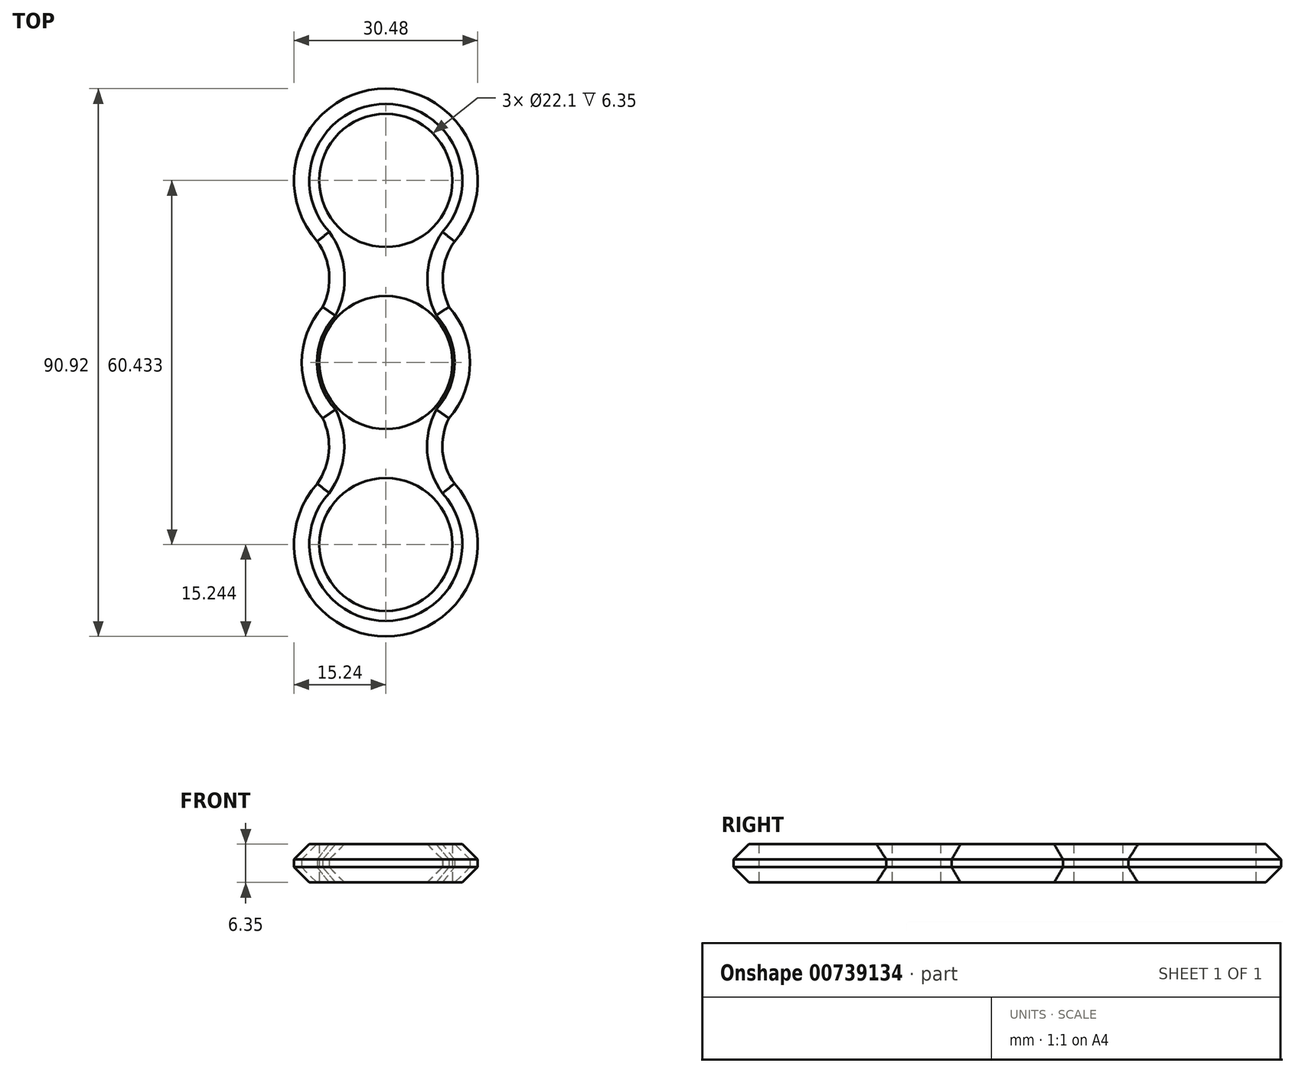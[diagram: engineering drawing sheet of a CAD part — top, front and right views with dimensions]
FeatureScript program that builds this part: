
annotation { "Feature Type Name" : "Feature", "Feature Type Description" : "" }
export const myFeature = defineFeature(function(context is Context, id is Id, definition is map)
    precondition{}
    {
        {
            var Q0;
            Q0=qCreatedBy(makeId("Top.planeOp"),FACE);
            var sketch = newSketch(context, id + "F0", { "sketchPlane" : qUnion([Q0])});
            skCircle(sketch, "E0", {"center": v(0, 0) * mm, "radius": 11.05 * mm});
            skCircle(sketch, "E1", {"center": v(0, 0) * mm, "radius": 13.97 * mm});
            skCircle(sketch, "E2", {"center": v(0, 30.22) * mm, "radius": 11.05 * mm});
            skCircle(sketch, "E3", {"center": v(0, 30.22) * mm, "radius": 15.24 * mm});
            skCircle(sketch, "E4.1.0", {"center": v(0, -30.22) * mm, "radius": 11.05 * mm});
            skCircle(sketch, "E4.1.1", {"center": v(0, -30.22) * mm, "radius": 15.24 * mm});
            skArc(sketch, "E5", {"start": v(11.4, 20.1) * mm, "mid": v(9.47, 14.79) * mm, "end": v(10.48, 9.24) * mm});
            skArc(sketch, "E6", {"start": v(-10.48, 9.24) * mm, "mid": v(-9.42, 14.8) * mm, "end": v(-11.4, 20.1) * mm});
            skArc(sketch, "E7.1.0", {"start": v(-11.4, -20.1) * mm, "mid": v(-9.47, -14.79) * mm, "end": v(-10.48, -9.24) * mm});
            skArc(sketch, "E7.1.1", {"start": v(10.48, -9.24) * mm, "mid": v(9.42, -14.8) * mm, "end": v(11.4, -20.1) * mm});
            skSolve(sketch);
        }
        {
            var Q0;
            Q0 = qSketchRegion(id + "F0", true);
            extrude(context, id + "F1", {"entities" : qUnion([Q0]), "depth" : 6.35 * mm, "offsetDistance" : 25.4 * mm});
        }
        {
            var Q0;
            Q0=makeQuery(id+"F1.opExtrude","CAP_EDGE",EDGE,{"disambiguationData":[OSD([sQuery(id+"F0.wireOp",EDGE,"E4.1.1")])],"isStart":true});
            var Q1;
            Q1=makeQuery(id+"F1.opExtrude","CAP_EDGE",EDGE,{"disambiguationData":[OSD([sQuery(id+"F0.wireOp",EDGE,"E7.1.0")])],"isStart":true});
            var Q2;
            {var subQ0=sQuery(id+"F0.wireOp",EDGE,"E1");Q2=makeQuery(id+"F1.opExtrude","CAP_EDGE",EDGE,{"disambiguationData":[OSD([subQ0]),TDD([makeQuery(id+"F0.imprint","IMPRINT",EDGE,{"disambiguationData":[TD([[makeQuery(id+"F0.imprint","INTERSECT",VERTEX,{"derivedFrom":[subQ0,sQuery(id+"F0.wireOp",EDGE,"E6")]}),-1.0]])],"derivedFrom":subQ0})])],"isStart":true});}
            var Q3;
            Q3=makeQuery(id+"F1.opExtrude","CAP_EDGE",EDGE,{"disambiguationData":[OSD([sQuery(id+"F0.wireOp",EDGE,"E6")])],"isStart":true});
            var Q4;
            Q4=makeQuery(id+"F1.opExtrude","CAP_EDGE",EDGE,{"disambiguationData":[OSD([sQuery(id+"F0.wireOp",EDGE,"E3")])],"isStart":true});
            var Q5;
            Q5=makeQuery(id+"F1.opExtrude","CAP_EDGE",EDGE,{"disambiguationData":[OSD([sQuery(id+"F0.wireOp",EDGE,"E5")])],"isStart":true});
            var Q6;
            {var subQ0=sQuery(id+"F0.wireOp",EDGE,"E1");Q6=makeQuery(id+"F1.opExtrude","CAP_EDGE",EDGE,{"disambiguationData":[OSD([subQ0]),TDD([makeQuery(id+"F0.imprint","IMPRINT",EDGE,{"disambiguationData":[TD([[makeQuery(id+"F0.imprint","INTERSECT",VERTEX,{"derivedFrom":[subQ0,sQuery(id+"F0.wireOp",EDGE,"E5")]}),1.0]])],"derivedFrom":subQ0})])],"isStart":true});}
            var Q7;
            Q7=makeQuery(id+"F1.opExtrude","CAP_EDGE",EDGE,{"disambiguationData":[OSD([sQuery(id+"F0.wireOp",EDGE,"E7.1.1")])],"isStart":true});
            chamfer(context, id + "F2", {"entities" : qUnion([Q0, Q1, Q2, Q3, Q4, Q5, Q6, Q7]), "width" : 2.54 * mm, "tangentPropagation" : true});
        }
        {
            var Q0;
            Q0=makeQuery(id+"F1.opExtrude","CAP_EDGE",EDGE,{"disambiguationData":[OSD([sQuery(id+"F0.wireOp",EDGE,"E3")])],"isStart":false});
            var Q1;
            Q1=makeQuery(id+"F1.opExtrude","CAP_EDGE",EDGE,{"disambiguationData":[OSD([sQuery(id+"F0.wireOp",EDGE,"E6")])],"isStart":false});
            var Q2;
            {var subQ0=sQuery(id+"F0.wireOp",EDGE,"E1");Q2=makeQuery(id+"F1.opExtrude","CAP_EDGE",EDGE,{"disambiguationData":[OSD([subQ0]),TDD([makeQuery(id+"F0.imprint","IMPRINT",EDGE,{"disambiguationData":[TD([[makeQuery(id+"F0.imprint","INTERSECT",VERTEX,{"derivedFrom":[subQ0,sQuery(id+"F0.wireOp",EDGE,"E6")]}),-1.0]])],"derivedFrom":subQ0})])],"isStart":false});}
            var Q3;
            Q3=makeQuery(id+"F1.opExtrude","CAP_EDGE",EDGE,{"disambiguationData":[OSD([sQuery(id+"F0.wireOp",EDGE,"E5")])],"isStart":false});
            var Q4;
            {var subQ0=sQuery(id+"F0.wireOp",EDGE,"E1");Q4=makeQuery(id+"F1.opExtrude","CAP_EDGE",EDGE,{"disambiguationData":[OSD([subQ0]),TDD([makeQuery(id+"F0.imprint","IMPRINT",EDGE,{"disambiguationData":[TD([[makeQuery(id+"F0.imprint","INTERSECT",VERTEX,{"derivedFrom":[subQ0,sQuery(id+"F0.wireOp",EDGE,"E5")]}),1.0]])],"derivedFrom":subQ0})])],"isStart":false});}
            var Q5;
            Q5=makeQuery(id+"F1.opExtrude","CAP_EDGE",EDGE,{"disambiguationData":[OSD([sQuery(id+"F0.wireOp",EDGE,"E4.1.1")])],"isStart":false});
            var Q6;
            Q6=makeQuery(id+"F1.opExtrude","CAP_EDGE",EDGE,{"disambiguationData":[OSD([sQuery(id+"F0.wireOp",EDGE,"E7.1.1")])],"isStart":false});
            var Q7;
            Q7=makeQuery(id+"F1.opExtrude","CAP_EDGE",EDGE,{"disambiguationData":[OSD([sQuery(id+"F0.wireOp",EDGE,"E7.1.0")])],"isStart":false});
            chamfer(context, id + "F3", {"entities" : qUnion([Q0, Q1, Q2, Q3, Q4, Q5, Q6, Q7]), "width" : 2.54 * mm, "tangentPropagation" : true});
        }
    });
